# Revit family: BVN_BDKF
name_source: partatom
category: Mechanical Equipment
units: mm (PartAtom-declared; Revit-internal decimal feet)

## family parameters
Always vertical = Yes
Cut with Voids When Loaded = No
OmniClass Number = 23.75.00.00
OmniClass Title = Climate Control (HVAC)
Part Type = Breaks Into
Room Calculation Point = No
Round Connector Dimension = Use Diameter
Shared = No
Work Plane-Based = No

## types (6) — shared parameters
Description = IGK
Frequency = 50 Hz
G = 61 mm
H = 375 mm  [stored 1.23031 ft]
Insulation Class = F
Manufacturer = Bahçıvan Elektrik Motor San. ve Tic. Ltd. Şti.
Material = <By Category>
Model = BGK
Protection Class = 44
URL = http://www.bahcivanmotor.com.tr
Voltage = 230 V
Voltage of Electrica Heater = 380 V

## per-type parameters (varying)
| type | A | Air Flow | B | C | Capacitor | Current x2 | D | E | Electrical Heater | F | Power x2 | Sound Pressure Level dB(A) | Speed ( d/d ) | Weight |
| BGK 75 | 1100 mm | 750.0 m³/h | 900 mm  [stored 2.95276 ft] | 315 mm  [stored 1.03346 ft] | 6 | 1 A | 220 mm  [stored 0.721785 ft] | 200 mm  [stored 0.656168 ft] | 3000 W | 455 mm | 140 W | 46 | 1440 | 80.00 kg |
| BGK 100 | 1200 mm | 1000.0 m³/h | 1000 mm  [stored 3.28084 ft] | 365 mm  [stored 1.19751 ft] | 8 | 1 A | 270 mm  [stored 0.885827 ft] | 300 mm | 3000 W | 455 mm | 200 W | 46 | 1420 | 113.00 kg |
| BGK 200 | 1500 mm  [stored 4.92126 ft] | 2000.0 m³/h | 1200 mm | 415 mm  [stored 1.36155 ft] | 10 | 2 A | 320 mm  [stored 1.04987 ft] | 400 mm  [stored 1.31234 ft] | 5000 W | 555 mm  [stored 1.82087 ft] | 310 W | 48 | 1430 | 150.00 kg |
| BGK 300 | 1700 mm  [stored 5.57743 ft] | 3000.0 m³/h | 1200 mm | 475 mm  [stored 1.5584 ft] | 10 | 3 A | 380 mm | 400 mm  [stored 1.31234 ft] | 8000 W | 555 mm  [stored 1.82087 ft] | 500 W | 49 | 1435 | 180.00 kg |
| BGK 400 | 1800 mm  [stored 5.90551 ft] | 4000.0 m³/h | 1300 mm  [stored 4.26509 ft] | 515 mm  [stored 1.68963 ft] | 16 | 4 A | 420 mm  [stored 1.37795 ft] | 400 mm  [stored 1.31234 ft] | 10000 W | 655 mm  [stored 2.14895 ft] | 780 W | 54 | 1280 | 200.00 kg |
| BGK 500 | 2000 mm  [stored 6.56168 ft] | 5000.0 m³/h | 1500 mm  [stored 4.92126 ft] | 615 mm  [stored 2.01772 ft] | 25 | 7 A | 520 mm  [stored 1.70604 ft] | 400 mm  [stored 1.31234 ft] | 13000 W | 855 mm  [stored 2.80512 ft] | 1550 W | 57 | 1250 | 230.00 kg |

note: [stored X ft] marks values corroborated as IEEE doubles in the binary element streams (Revit-internal decimal feet)

## geometry (parser evidence)
native form markers: Sweep x2
no freeform markers — native parametric forms only
